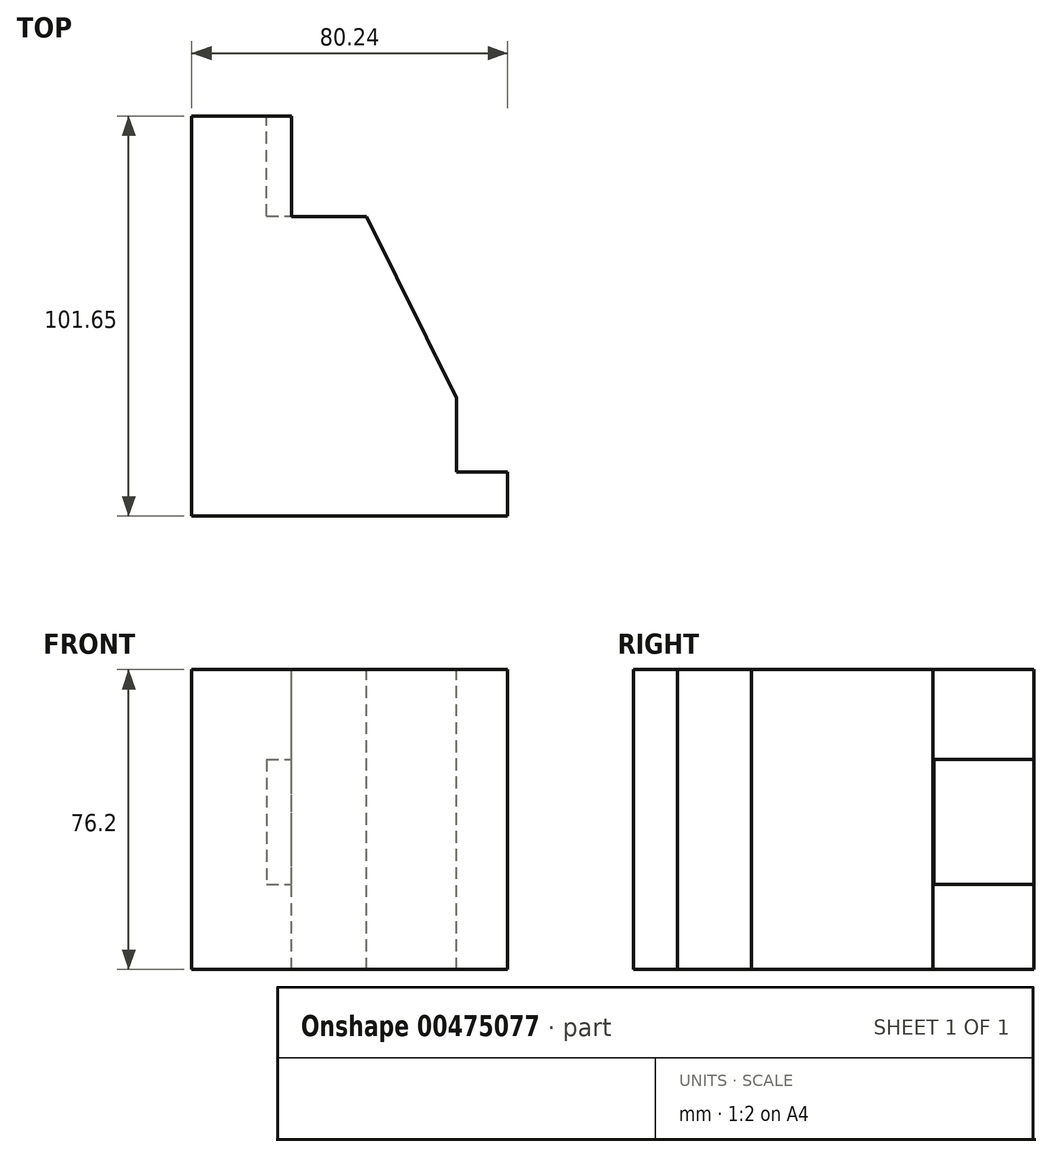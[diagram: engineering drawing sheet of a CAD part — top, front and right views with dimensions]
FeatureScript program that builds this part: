
annotation { "Feature Type Name" : "Feature", "Feature Type Description" : "" }
export const myFeature = defineFeature(function(context is Context, id is Id, definition is map)
    precondition{}
    {
        {
            var Q0;
            Q0=qCreatedBy(makeId("Top.planeOp"),FACE);
            var sketch = newSketch(context, id + "F0", { "sketchPlane" : qUnion([Q0])});
            skLineSegment(sketch, "E0", {"start": v(-51.17, 53.5) * mm, "end": v(-51.17, -48.15) * mm});
            skLineSegment(sketch, "E1", {"start": v(-51.17, -48.15) * mm, "end": v(37.91, -48.15) * mm});
            skLineSegment(sketch, "E2", {"start": v(37.91, -48.15) * mm, "end": v(37.91, 53.5) * mm});
            skLineSegment(sketch, "E3", {"start": v(37.91, 53.5) * mm, "end": v(-51.17, 53.5) * mm});
            skSolve(sketch);
        }
        {
            var Q0;
            Q0 = qSketchRegion(id + "F0", true);
            extrude(context, id + "F1", {"entities" : qUnion([Q0]), "depth" : 76.2 * mm});
        }
        {
            var Q0;
            Q0=makeQuery(id+"F1.opExtrude","CAP_FACE",FACE,{"disambiguationData":[OSD([sQuery(id+"F0.wireOp",EDGE,"E0"),sQuery(id+"F0.wireOp",EDGE,"E1"),sQuery(id+"F0.wireOp",EDGE,"E2"),sQuery(id+"F0.wireOp",EDGE,"E3")])],"isStart":false});
            var sketch = newSketch(context, id + "F2", { "sketchPlane" : qUnion([Q0])});
            skLineSegment(sketch, "E4", {"start": v(-25.82, 53.5) * mm, "end": v(-25.82, 27.91) * mm});
            skLineSegment(sketch, "E5", {"start": v(-25.82, 27.91) * mm, "end": v(-6.75, 27.91) * mm});
            skLineSegment(sketch, "E6", {"start": v(-6.75, 27.91) * mm, "end": v(16.05, -18.14) * mm});
            skLineSegment(sketch, "E7", {"start": v(16.05, -18.14) * mm, "end": v(16.05, -36.98) * mm});
            skLineSegment(sketch, "E8", {"start": v(16.05, -36.98) * mm, "end": v(29.07, -36.98) * mm});
            skLineSegment(sketch, "E9", {"start": v(29.07, -36.98) * mm, "end": v(29.07, -48.15) * mm});
            skLineSegment(sketch, "E10", {"start": v(37.91, 53.5) * mm, "end": v(37.91, -48.15) * mm});
            skLineSegment(sketch, "E11", {"start": v(37.91, -48.15) * mm, "end": v(29.07, -48.15) * mm});
            skLineSegment(sketch, "E12", {"start": v(-25.82, 53.5) * mm, "end": v(37.91, 53.5) * mm});
            skLineSegment(sketch, "E13", {"start": v(37.91, -48.15) * mm, "end": v(31.17, -48.15) * mm});
            skLineSegment(sketch, "E14", {"start": v(31.17, -48.15) * mm, "end": v(29.07, -48.15) * mm});
            skSolve(sketch);
        }
        {
            var Q0;
            Q0=makeQuery(id+"F2.imprint","IMPRINT",FACE,{"disambiguationData":[TD([[makeQuery(id+"F2.imprint","IMPRINT",EDGE,{"derivedFrom":sQuery(id+"F2.wireOp",EDGE,"E4")}),1.0]])]});
            extrude(context, id + "F3", {"entities" : qUnion([Q0]), "operationType" : NewBodyOperationType.REMOVE, "endBound" : BoundingType.THROUGH_ALL, "oppositeDirection" : true, "depth" : 25.4 * mm});
        }
        {
            var Q0;
            Q0=qCreatedBy(makeId("Right.planeOp"),FACE);
            var sketch = newSketch(context, id + "F4", { "sketchPlane" : qUnion([Q0])});
            skCircle(sketch, "E15", {"center": v(0, 59.54) * mm, "radius": 10.69 * mm});
            skSolve(sketch);
        }
        {
            var Q0;
            Q0 = qSketchRegion(id + "F4", true);
            var Q1;
            Q1=makeQuery(id+"F3.boolean.opBoolean","COPY",FACE,{"derivedFrom":makeQuery(id+"F3.opExtrude","SWEPT_FACE",FACE,{"disambiguationData":[OSD([sQuery(id+"F2.wireOp",EDGE,"E6")])]})});
            extrude(context, id + "F5", {"entities" : qUnion([Q0, Q1]), "operationType" : NewBodyOperationType.ADD, "oppositeDirection" : true, "depth" : 12.7 * mm});
        }
        {
            var Q0;
            Q0=qCreatedBy(makeId("Right.planeOp"),FACE);
            var sketch = newSketch(context, id + "F6", { "sketchPlane" : qUnion([Q0])});
            skCircle(sketch, "E16", {"center": v(0, 13.26) * mm, "radius": 11.55 * mm});
            skSolve(sketch);
        }
        {
            var Q0;
            Q0 = qSketchRegion(id + "F6", true);
            extrude(context, id + "F7", {"entities" : qUnion([Q0]), "operationType" : NewBodyOperationType.ADD, "oppositeDirection" : true, "depth" : 25.4 * mm});
        }
        {
            var Q0;
            Q0=makeQuery(id+"F1.opExtrude","SWEPT_FACE",FACE,{"disambiguationData":[OSD([sQuery(id+"F0.wireOp",EDGE,"E3")])]});
            var sketch = newSketch(context, id + "F8", { "sketchPlane" : qUnion([Q0])});
            skLineSegment(sketch, "E17.bottom", {"start": v(32.17, 53.34) * mm, "end": v(25.82, 53.34) * mm});
            skLineSegment(sketch, "E17.top", {"start": v(32.17, 21.59) * mm, "end": v(25.82, 21.59) * mm});
            skLineSegment(sketch, "E17.left", {"start": v(32.17, 53.34) * mm, "end": v(32.17, 21.59) * mm});
            skLineSegment(sketch, "E17.right", {"start": v(25.82, 53.34) * mm, "end": v(25.82, 21.6) * mm});
            skSolve(sketch);
        }
        {
            var Q0;
            Q0 = qSketchRegion(id + "F8", true);
            extrude(context, id + "F9", {"entities" : qUnion([Q0]), "operationType" : NewBodyOperationType.REMOVE, "oppositeDirection" : true, "depth" : 25.4 * mm});
        }
    });
